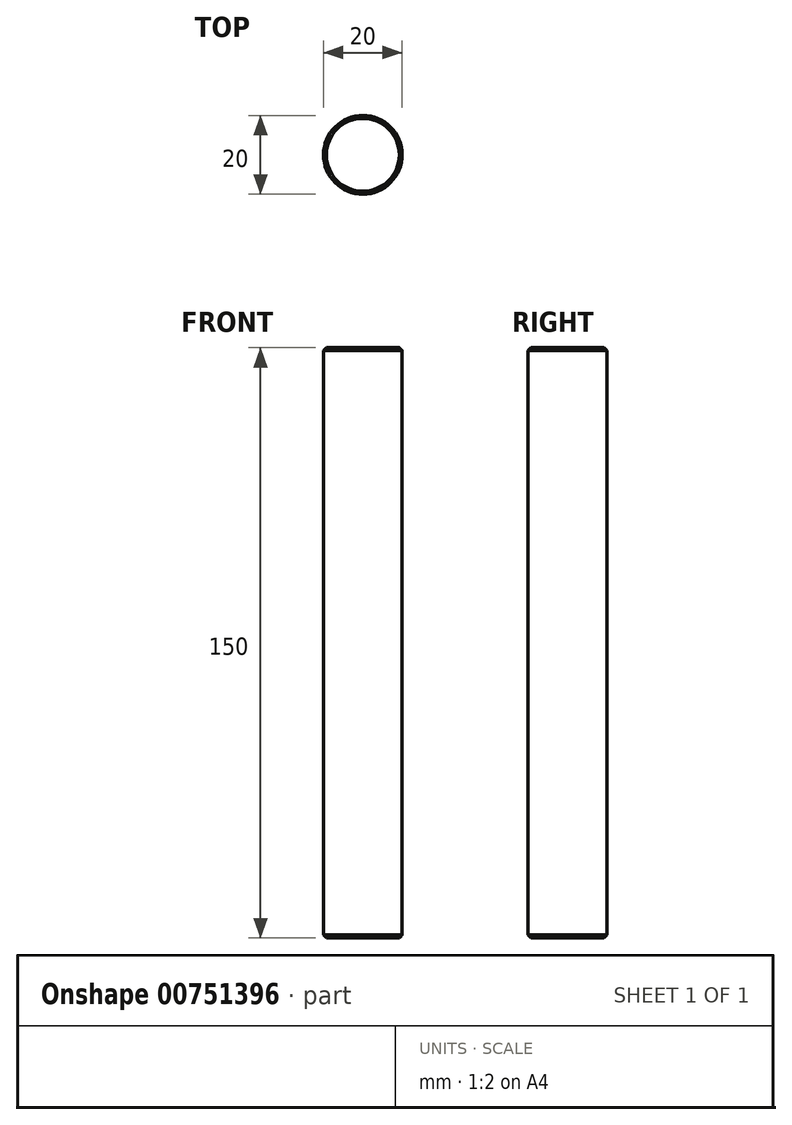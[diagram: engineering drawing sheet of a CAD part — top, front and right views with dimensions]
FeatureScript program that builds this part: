
annotation { "Feature Type Name" : "Feature", "Feature Type Description" : "" }
export const myFeature = defineFeature(function(context is Context, id is Id, definition is map)
    precondition{}
    {
        {
            var Q0;
            Q0=qCreatedBy(makeId("Top.planeOp"),FACE);
            var sketch = newSketch(context, id + "F0", { "sketchPlane" : qUnion([Q0])});
            skCircle(sketch, "E0", {"center": v(0, 0) * mm, "radius": 10 * mm});
            skSolve(sketch);
        }
        {
            var Q0;
            Q0=makeQuery(id+"F0.imprint","IMPRINT",FACE,{"disambiguationData":[TD([[makeQuery(id+"F0.imprint","IMPRINT",EDGE,{"derivedFrom":sQuery(id+"F0.wireOp",EDGE,"E0")}),1.0]])]});
            extrude(context, id + "F1", {"entities" : qUnion([Q0]), "depth" : 150 * mm, "offsetDistance" : 25 * mm});
        }
        {
            var Q0;
            Q0=makeQuery(id+"F1.opExtrude","CAP_EDGE",EDGE,{"disambiguationData":[OSD([sQuery(id+"F0.wireOp",EDGE,"E0")])],"isStart":false});
            var Q1;
            Q1=makeQuery(id+"F1.opExtrude","CAP_EDGE",EDGE,{"disambiguationData":[OSD([sQuery(id+"F0.wireOp",EDGE,"E0")])],"isStart":true});
            chamfer(context, id + "F2", {"entities" : qUnion([Q0, Q1]), "width" : .75 * mm});
        }
    });
